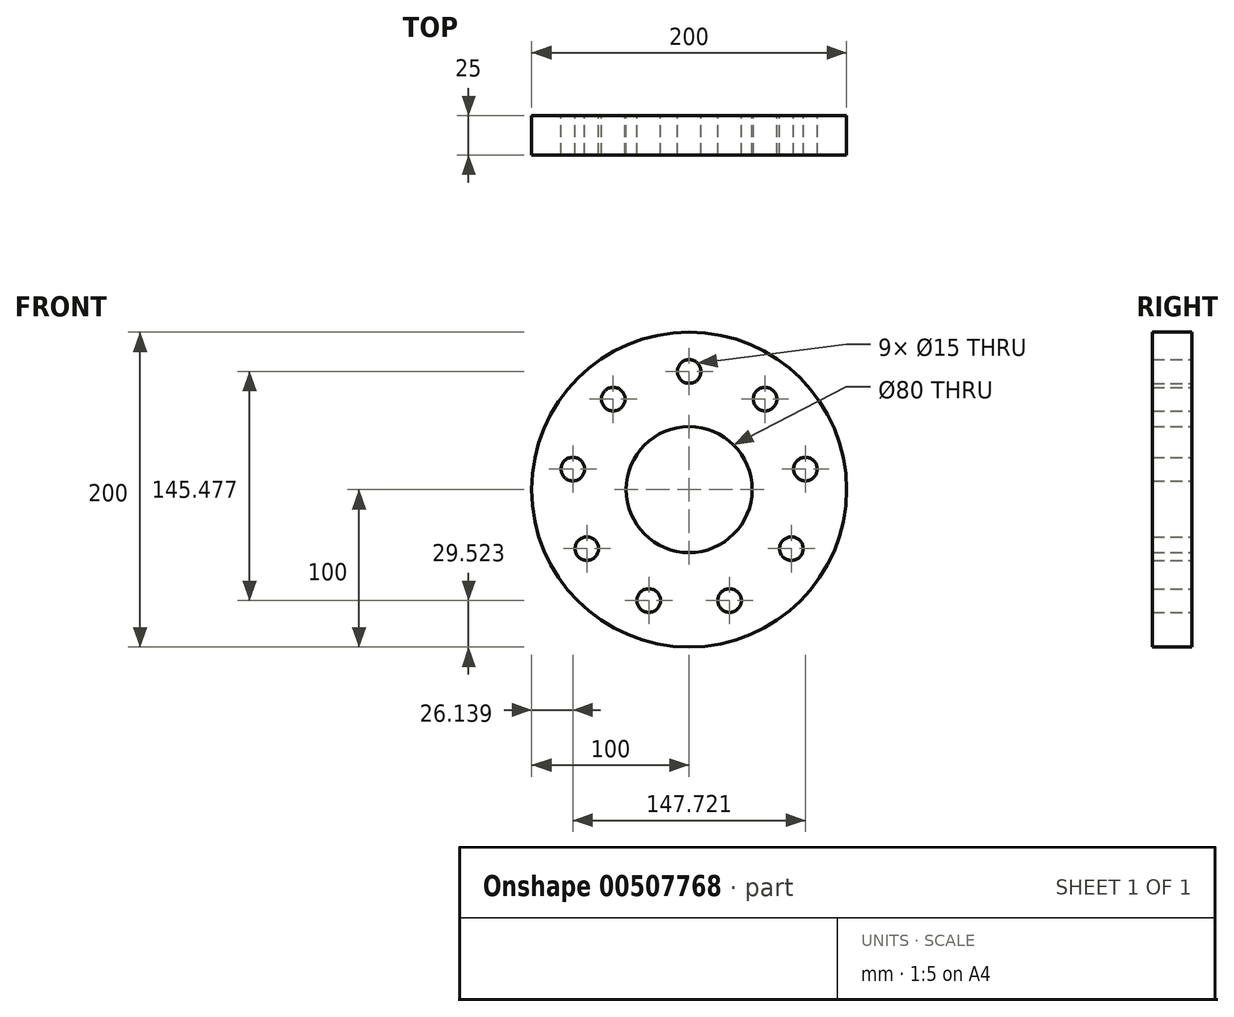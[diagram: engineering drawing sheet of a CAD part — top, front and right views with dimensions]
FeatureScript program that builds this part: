
annotation { "Feature Type Name" : "Feature", "Feature Type Description" : "" }
export const myFeature = defineFeature(function(context is Context, id is Id, definition is map)
    precondition{}
    {
        {
            var Q0;
            Q0=qCreatedBy(makeId("Front.planeOp"),FACE);
            var sketch = newSketch(context, id + "F0", { "sketchPlane" : qUnion([Q0])});
            skCircle(sketch, "E0", {"center": v(0, 0) * mm, "radius": 100 * mm});
            skCircle(sketch, "E1", {"center": v(0, 75) * mm, "radius": 7.5 * mm});
            skCircle(sketch, "E2.1.0", {"center": v(-48.2, 57.45) * mm, "radius": 7.5 * mm});
            skCircle(sketch, "E2.2.0", {"center": v(-73.86, 13.02) * mm, "radius": 7.5 * mm});
            skCircle(sketch, "E2.3.0", {"center": v(-64.95, -37.5) * mm, "radius": 7.5 * mm});
            skCircle(sketch, "E2.4.0", {"center": v(-25.65, -70.48) * mm, "radius": 7.5 * mm});
            skCircle(sketch, "E2.5.0", {"center": v(25.65, -70.48) * mm, "radius": 7.5 * mm});
            skCircle(sketch, "E2.6.0", {"center": v(64.95, -37.5) * mm, "radius": 7.5 * mm});
            skCircle(sketch, "E2.7.0", {"center": v(73.86, 13.02) * mm, "radius": 7.5 * mm});
            skCircle(sketch, "E2.8.0", {"center": v(48.2, 57.45) * mm, "radius": 7.5 * mm});
            skCircle(sketch, "E3", {"center": v(0, 0) * mm, "radius": 40 * mm});
            skSolve(sketch);
        }
        {
            var Q0;
            Q0=makeQuery(id+"F0.imprint","IMPRINT",FACE,{"disambiguationData":[TD([[makeQuery(id+"F0.imprint","IMPRINT",EDGE,{"derivedFrom":sQuery(id+"F0.wireOp",EDGE,"E0")}),1.0]])]});
            extrude(context, id + "F1", {"entities" : qUnion([Q0]), "depth" : 25 * mm});
        }
    });
